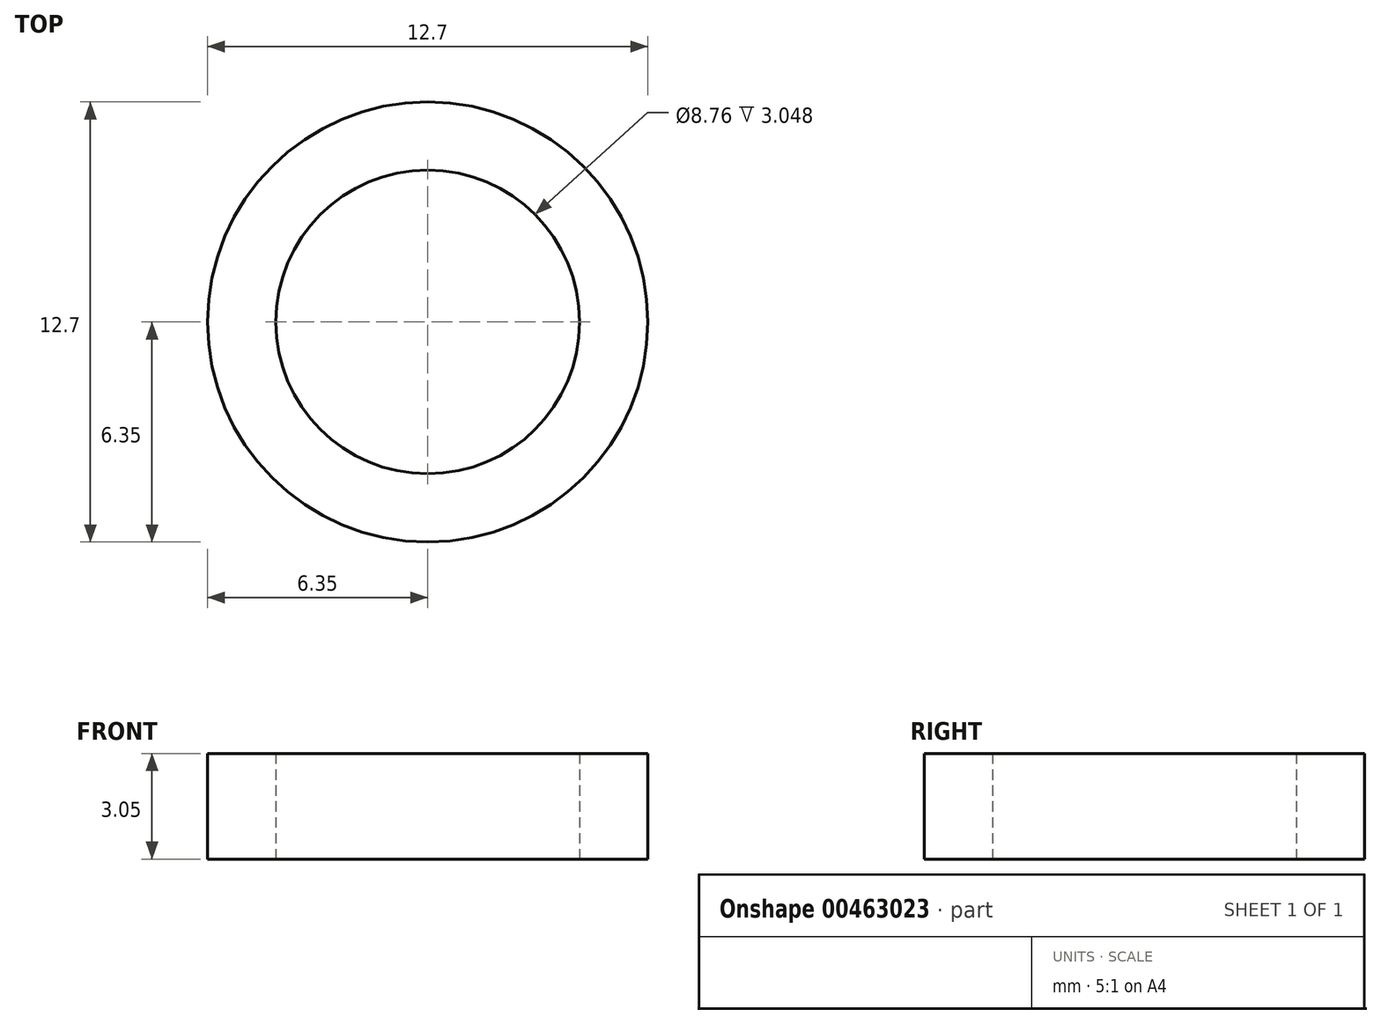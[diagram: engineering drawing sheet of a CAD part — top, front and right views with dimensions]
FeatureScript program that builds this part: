
annotation { "Feature Type Name" : "Feature", "Feature Type Description" : "" }
export const myFeature = defineFeature(function(context is Context, id is Id, definition is map)
    precondition{}
    {
        {
            var Q0;
            Q0=qCreatedBy(makeId("Top.planeOp"),FACE);
            var sketch = newSketch(context, id + "F0", { "sketchPlane" : qUnion([Q0])});
            skCircle(sketch, "E0", {"center": v(0, 0) * mm, "radius": 4.38 * mm});
            skCircle(sketch, "E1", {"center": v(0, 0) * mm, "radius": 6.35 * mm});
            skSolve(sketch);
        }
        {
            var Q0;
            Q0=makeQuery(id+"F0.imprint","IMPRINT",FACE,{"disambiguationData":[TD([[makeQuery(id+"F0.imprint","IMPRINT",EDGE,{"derivedFrom":sQuery(id+"F0.wireOp",EDGE,"E0")}),-1.0]])]});
            extrude(context, id + "F1", {"entities" : qUnion([Q0]), "depth" : 3.05 * mm});
        }
    });
